FCSTD DOCUMENT  (FreeCAD 1.0R39109 (Git))
Label: female static edge cut
License: All rights reserved
LicenseURL: https://en.wikipedia.org/wiki/All_rights_reserved
objects: Sketcher::SketchObject×1
note: 2 computed .brp shape members not serialized (recipe doc carries the construction recipe); baked Part::Feature solids carry a one-line shape summary decoded from their .brp

FEATURE [Sketcher::SketchObject] Sketch
  ArcFitTolerance = 1e-06
  FullyConstrained = true
  MakeInternals = false
  sketch-geometry (12):
    g0: LineSegment StartX=5 StartY=4.4e-15 StartZ=0 EndX=45 EndY=4.4e-15 EndZ=0
    g1: LineSegment StartX=50 StartY=5 StartZ=0 EndX=50 EndY=105 EndZ=0
    g2: LineSegment StartX=45 StartY=110 StartZ=0 EndX=5 EndY=110 EndZ=0
    g3: LineSegment StartX=0 StartY=105 StartZ=0 EndX=0 EndY=5 EndZ=0
    g4: ArcOfCircle CenterX=5 CenterY=105 CenterZ=0 NormalX=0 NormalY=0 NormalZ=1 AngleXU=0 Radius=5 StartAngle=1.5708 EndAngle=3.14159
    g5: GeomPoint [constr] X=0 Y=110 Z=0
    g6: ArcOfCircle CenterX=45 CenterY=105 CenterZ=0 NormalX=0 NormalY=0 NormalZ=1 AngleXU=0 Radius=5 StartAngle=-9e-16 EndAngle=1.5708
    g7: GeomPoint [constr] X=50 Y=110 Z=0
    g8: ArcOfCircle CenterX=5 CenterY=5 CenterZ=0 NormalX=0 NormalY=0 NormalZ=1 AngleXU=0 Radius=5 StartAngle=3.14159 EndAngle=4.71239
    g9: GeomPoint [constr] X=0 Y=0 Z=0
    g10: ArcOfCircle CenterX=45 CenterY=5 CenterZ=0 NormalX=0 NormalY=0 NormalZ=1 AngleXU=0 Radius=5 StartAngle=4.71239 EndAngle=6.28319
    g11: GeomPoint [constr] X=50 Y=0 Z=0
  constraints (27):
    c: Horizontal(g0)
    c: Horizontal(g2)
    c: Vertical(g1)
    c: Vertical(g3)
    c: Coincident(g9,g-1)
    c: DistanceY(g9,g5) = 110
    c: DistanceX(g9,g11) = 50
    c: PointOnObject(g5,g2)
    c: PointOnObject(g5,g3)
    c: Tangent(g2,g4) = -1.5708
    c: Tangent(g3,g4) = -1.5708
    c: PointOnObject(g7,g1)
    c: PointOnObject(g7,g2)
    c: Tangent(g1,g6) = -1.5708
    c: Tangent(g2,g6) = -1.5708
    c: PointOnObject(g9,g3)
    c: PointOnObject(g9,g0)
    c: Tangent(g3,g8) = -1.5708
    c: Tangent(g0,g8) = -1.5708
    c: PointOnObject(g11,g1)
    c: PointOnObject(g11,g0)
    c: Tangent(g1,g10) = -1.5708
    c: Tangent(g0,g10) = -1.5708
    c: Radius(g6) = 5
    c: Radius(g4) = 5
    c: Radius(g8) = 5
    c: Radius(g10) = 5
